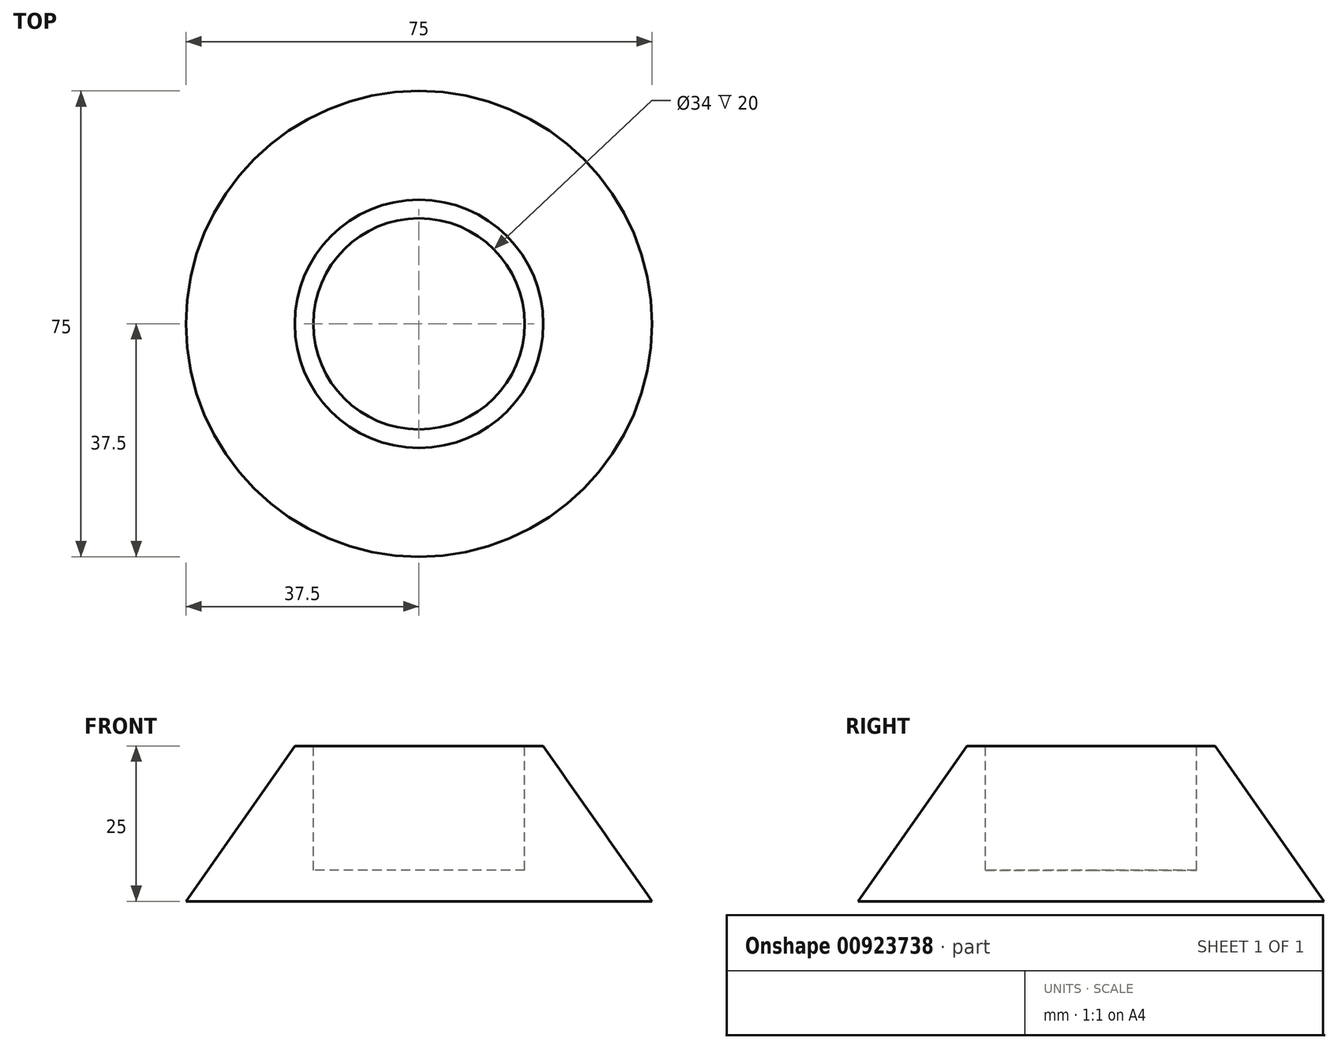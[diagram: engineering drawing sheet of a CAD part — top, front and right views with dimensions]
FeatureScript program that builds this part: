
annotation { "Feature Type Name" : "Feature", "Feature Type Description" : "" }
export const myFeature = defineFeature(function(context is Context, id is Id, definition is map)
    precondition{}
    {
        {
            var Q0;
            Q0=qCreatedBy(makeId("Top.planeOp"),FACE);
            var sketch = newSketch(context, id + "F0", { "sketchPlane" : qUnion([Q0]), "disableImprinting" : false});
            skCircle(sketch, "E0", {"center": v(0, 0) * mm, "radius": 37.5 * mm});
            skSolve(sketch);
        }
        {
            var Q0;
            Q0 = qSketchRegion(id + "F0", true);
            extrude(context, id + "F1", {"entities" : qUnion([Q0]), "flatOperationType" : FlatOperationType.REMOVE, "depth" : 25 * mm, "offsetDistance" : 25 * mm, "hasDraft" : true, "draftAngle" : 35 * degree, "draftPullDirection" : true, "domain" : OperationDomain.MODEL});
        }
        {
            var Q0;
            Q0=makeQuery(id+"F1.opExtrude","CAP_FACE",FACE,{"disambiguationData":[OSD([sQuery(id+"F0.wireOp",EDGE,"E0")])],"isStart":false});
            var sketch = newSketch(context, id + "F2", { "sketchPlane" : qUnion([Q0]), "disableImprinting" : false});
            skCircle(sketch, "E1", {"center": v(0, 0) * mm, "radius": 17 * mm});
            skSolve(sketch);
        }
        {
            var Q0;
            Q0 = qSketchRegion(id + "F2", true);
            extrude(context, id + "F3", {"entities" : qUnion([Q0]), "operationType" : NewBodyOperationType.REMOVE, "oppositeDirection" : true, "depth" : 20 * mm, "offsetDistance" : 25 * mm});
        }
    });
